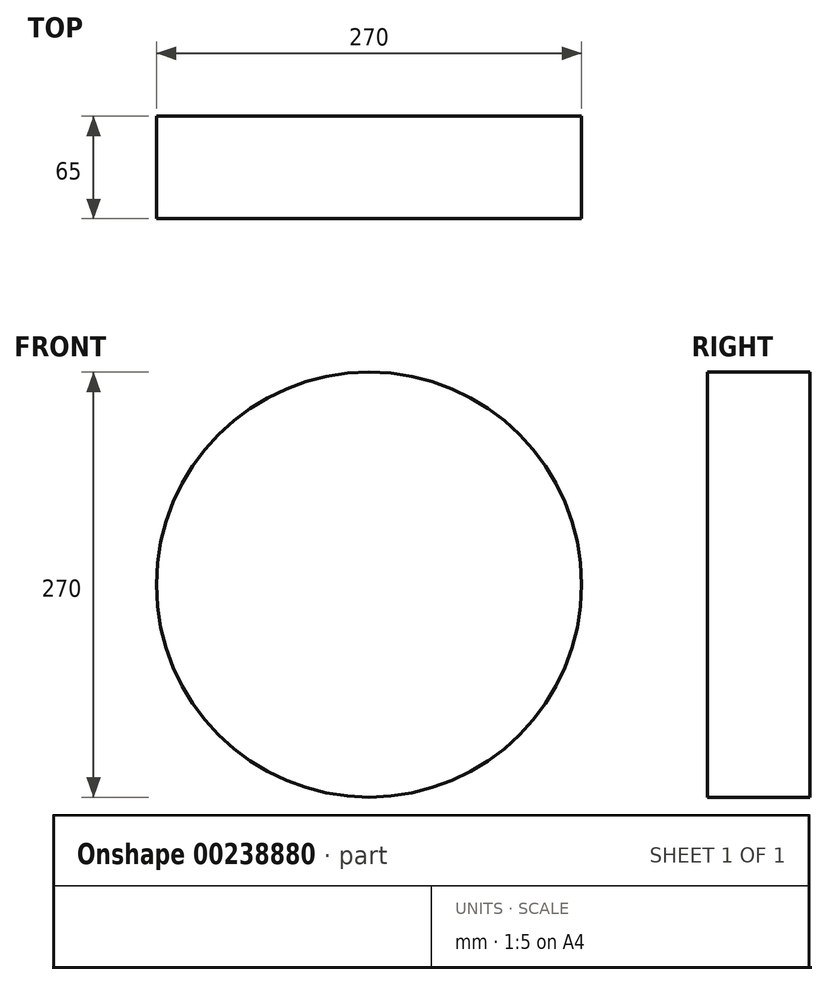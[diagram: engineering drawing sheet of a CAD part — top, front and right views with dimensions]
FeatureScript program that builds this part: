
annotation { "Feature Type Name" : "Feature", "Feature Type Description" : "" }
export const myFeature = defineFeature(function(context is Context, id is Id, definition is map)
    precondition{}
    {
        {
            var Q0;
            Q0=qCreatedBy(makeId("Front.planeOp"), FACE);
            var sketch = newSketch(context, id + "F0", { "sketchPlane" : qUnion([Q0])});
            skCircle(sketch, "E0", {"center": v(0, 0) * mm, "radius": 135 * mm});
            skSolve(sketch);
        }
        {
            var Q0;
            Q0 = qSketchRegion(id + "F0", true);
            extrude(context, id + "F1", {"entities" : qUnion([Q0]), "depth" : 65 * mm, "offsetDistance" : 25 * mm});
        }
    });
